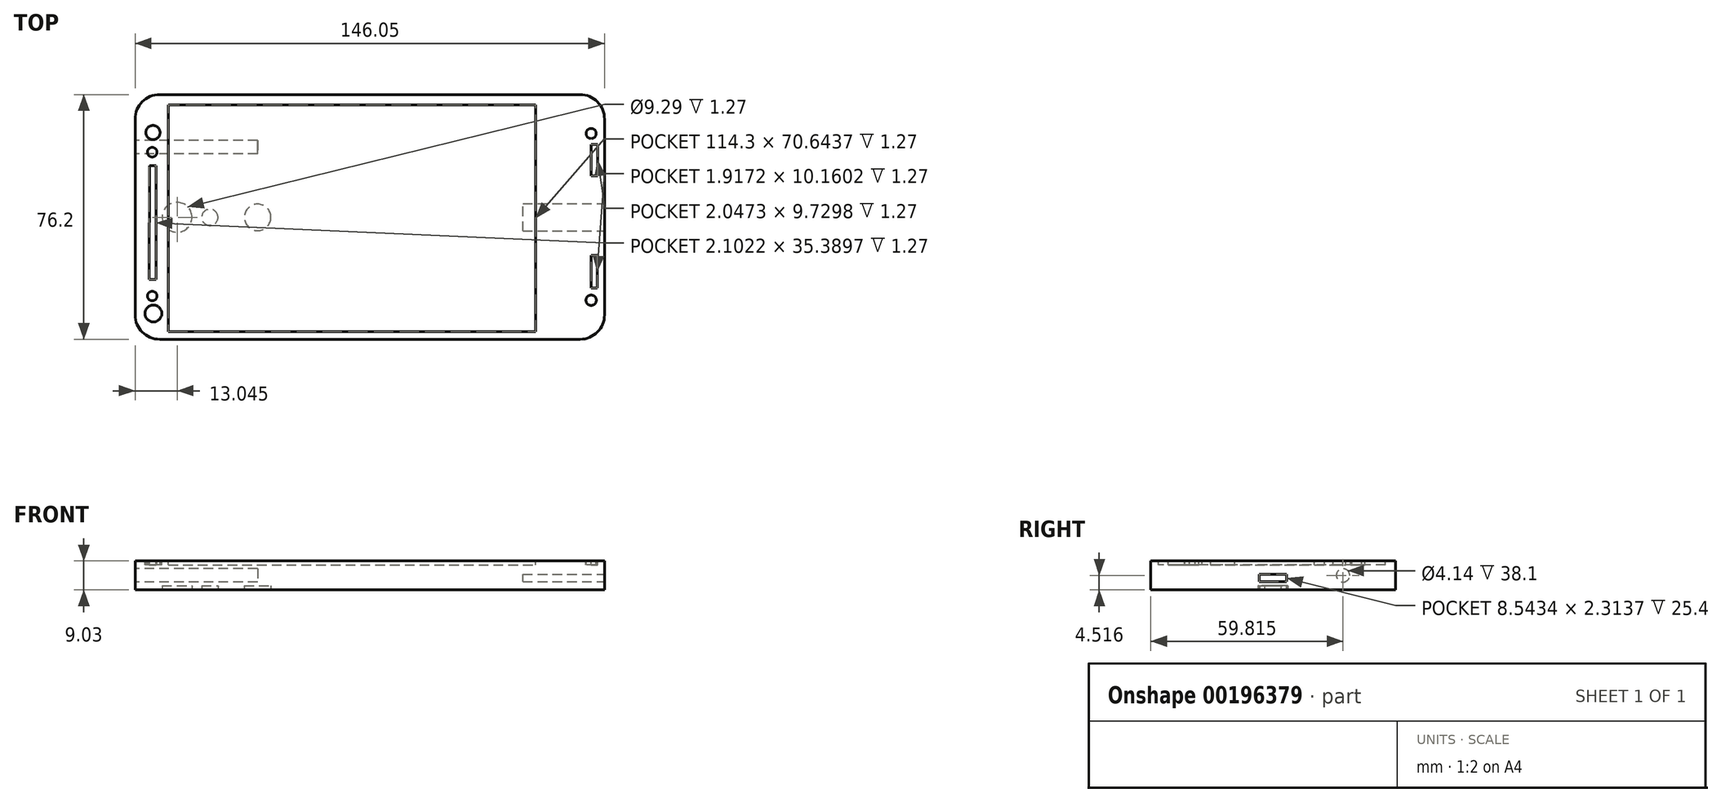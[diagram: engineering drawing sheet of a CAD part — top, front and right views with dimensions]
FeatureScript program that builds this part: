
annotation { "Feature Type Name" : "Feature", "Feature Type Description" : "" }
export const myFeature = defineFeature(function(context is Context, id is Id, definition is map)
    precondition{}
    {
        {
            var Q0;
            Q0=qCreatedBy(makeId("Top.planeOp"),FACE);
            var sketch = newSketch(context, id + "F0", { "sketchPlane" : qUnion([Q0])});
            skLineSegment(sketch, "E0.bottom", {"start": v(-70.09, 38.22) * mm, "end": v(75.96, 38.22) * mm});
            skLineSegment(sketch, "E0.top", {"start": v(-70.09, -37.98) * mm, "end": v(75.96, -37.98) * mm});
            skLineSegment(sketch, "E0.left", {"start": v(-70.09, 38.22) * mm, "end": v(-70.09, -37.98) * mm});
            skLineSegment(sketch, "E0.right", {"start": v(75.96, 38.22) * mm, "end": v(75.96, -37.98) * mm});
            skSolve(sketch);
        }
        {
            var Q0;
            Q0=qSketchRegion(id+"F0",true);
            extrude(context, id + "F1", {"entities" : qUnion([Q0]), "depth" : 9.03 * mm});
        }
        {
            var Q0;
            Q0=makeQuery(id+"F1.opExtrude","SWEPT_EDGE",EDGE,{"disambiguationData":[OSD([sQuery(id+"F0.wireOp",EDGE,"E0.top"),sQuery(id+"F0.wireOp",EDGE,"E0.right")])]});
            var Q1;
            Q1=makeQuery(id+"F1.opExtrude","SWEPT_EDGE",EDGE,{"disambiguationData":[OSD([sQuery(id+"F0.wireOp",EDGE,"E0.top"),sQuery(id+"F0.wireOp",EDGE,"E0.left")])]});
            var Q2;
            Q2=makeQuery(id+"F1.opExtrude","SWEPT_EDGE",EDGE,{"disambiguationData":[OSD([sQuery(id+"F0.wireOp",EDGE,"E0.bottom"),sQuery(id+"F0.wireOp",EDGE,"E0.left")])]});
            var Q3;
            Q3=makeQuery(id+"F1.opExtrude","SWEPT_EDGE",EDGE,{"disambiguationData":[OSD([sQuery(id+"F0.wireOp",EDGE,"E0.bottom"),sQuery(id+"F0.wireOp",EDGE,"E0.right")])]});
            fillet(context, id + "F2", {"entities" : qUnion([Q0, Q1, Q2, Q3]), "radius" : 7.62 * mm, "tangentPropagation" : true, "allowEdgeOverflow" : false});
        }
        {
            var Q0;
            Q0=makeQuery(id+"F1.opExtrude","SWEPT_FACE",FACE,{"disambiguationData":[OSD([sQuery(id+"F0.wireOp",EDGE,"E0.right")])]});
            var sketch = newSketch(context, id + "F3", { "sketchPlane" : qUnion([Q0])});
            skPoint(sketch, "E1.endSnap0", {"position": v(-30.36, 4.52) * mm});
            skLineSegment(sketch, "E2", {"start": v(-4.27, 2.5) * mm, "end": v(4.27, 2.5) * mm});
            skLineSegment(sketch, "E3", {"start": v(-4.27, 2.5) * mm, "end": v(-4.27, 4.81) * mm});
            skLineSegment(sketch, "E4", {"start": v(4.27, 2.5) * mm, "end": v(4.27, 4.81) * mm});
            skPoint(sketch, "E5.centerSnap0", {"position": v(0, 2.5) * mm});
            skLineSegment(sketch, "E6", {"start": v(-4.27, 4.81) * mm, "end": v(4.27, 4.81) * mm});
            skSolve(sketch);
        }
        {
            var Q0;
            Q0=qSketchRegion(id+"F3",true);
            extrude(context, id + "F4", {"entities" : qUnion([Q0]), "operationType" : NewBodyOperationType.REMOVE, "oppositeDirection" : true, "depth" : 25.4 * mm});
        }
        {
            var Q0;
            Q0=makeQuery(id+"F1.opExtrude","SWEPT_FACE",FACE,{"disambiguationData":[OSD([sQuery(id+"F0.wireOp",EDGE,"E0.left")])]});
            var sketch = newSketch(context, id + "F5", { "sketchPlane" : qUnion([Q0])});
            skCircle(sketch, "E7", {"center": v(-21.84, 4.52) * mm, "radius": 2.07 * mm});
            skPoint(sketch, "E7.centerSnap0", {"position": v(-30.6, 4.52) * mm});
            skSolve(sketch);
        }
        {
            var Q0;
            Q0=qSketchRegion(id+"F5",true);
            extrude(context, id + "F6", {"entities" : qUnion([Q0]), "operationType" : NewBodyOperationType.REMOVE, "oppositeDirection" : true, "depth" : 2.54 * mm});
        }
        {
            var Q0;
            Q0=qSketchRegion(id+"F5",true);
            extrude(context, id + "F7", {"entities" : qUnion([Q0]), "operationType" : NewBodyOperationType.REMOVE, "oppositeDirection" : true, "depth" : 38.1 * mm});
        }
        {
            var Q0;
            Q0=makeQuery(id+"F1.opExtrude","CAP_FACE",FACE,{"disambiguationData":[OSD([sQuery(id+"F0.wireOp",EDGE,"E0.bottom"),sQuery(id+"F0.wireOp",EDGE,"E0.top"),sQuery(id+"F0.wireOp",EDGE,"E0.left"),sQuery(id+"F0.wireOp",EDGE,"E0.right")])],"isStart":false});
            var sketch = newSketch(context, id + "F8", { "sketchPlane" : qUnion([Q0])});
            skLineSegment(sketch, "E8.bottom", {"start": v(-59.77, 35.04) * mm, "end": v(54.53, 35.04) * mm});
            skLineSegment(sketch, "E8.top", {"start": v(-59.77, -35.6) * mm, "end": v(54.53, -35.6) * mm});
            skLineSegment(sketch, "E8.left", {"start": v(-59.77, 35.04) * mm, "end": v(-59.77, -35.6) * mm});
            skLineSegment(sketch, "E8.right", {"start": v(54.53, 35.04) * mm, "end": v(54.53, -35.6) * mm});
            skSolve(sketch);
        }
        {
            var Q0;
            Q0=qSketchRegion(id+"F8",true);
            extrude(context, id + "F9", {"entities" : qUnion([Q0]), "operationType" : NewBodyOperationType.REMOVE, "oppositeDirection" : true, "depth" : 1.27 * mm});
        }
        {
            var Q0;
            Q0=makeQuery(id+"F1.opExtrude","CAP_FACE",FACE,{"disambiguationData":[OSD([sQuery(id+"F0.wireOp",EDGE,"E0.bottom"),sQuery(id+"F0.wireOp",EDGE,"E0.top"),sQuery(id+"F0.wireOp",EDGE,"E0.left"),sQuery(id+"F0.wireOp",EDGE,"E0.right")])],"isStart":false});
            var sketch = newSketch(context, id + "F10", { "sketchPlane" : qUnion([Q0])});
            skCircle(sketch, "E9", {"center": v(-64.55, 26.4) * mm, "radius": 2.21 * mm});
            skCircle(sketch, "E10", {"center": v(-64.78, 20.28) * mm, "radius": 1.5 * mm});
            skCircle(sketch, "E11", {"center": v(71.8, 26.1) * mm, "radius": 1.57 * mm});
            skCircle(sketch, "E12", {"center": v(71.8, -25.83) * mm, "radius": 1.61 * mm});
            skCircle(sketch, "E13", {"center": v(-64.42, -29.95) * mm, "radius": 2.61 * mm});
            skCircle(sketch, "E14", {"center": v(-64.78, -24.52) * mm, "radius": 1.48 * mm});
            skLineSegment(sketch, "E15", {"start": v(-65.67, 16.05) * mm, "end": v(-63.61, 16.05) * mm});
            skLineSegment(sketch, "E16", {"start": v(-63.61, 16.05) * mm, "end": v(-63.61, -19.34) * mm});
            skLineSegment(sketch, "E17", {"start": v(-63.61, -19.34) * mm, "end": v(-65.71, -19.34) * mm});
            skLineSegment(sketch, "E18", {"start": v(-65.71, -19.34) * mm, "end": v(-65.67, 16.05) * mm});
            skLineSegment(sketch, "E19", {"start": v(71.8, 22.68) * mm, "end": v(73.85, 22.68) * mm});
            skLineSegment(sketch, "E20", {"start": v(73.85, 22.68) * mm, "end": v(73.85, 12.95) * mm});
            skLineSegment(sketch, "E21", {"start": v(73.85, 12.95) * mm, "end": v(71.8, 12.95) * mm});
            skLineSegment(sketch, "E22", {"start": v(71.8, 12.95) * mm, "end": v(71.8, 22.68) * mm});
            skLineSegment(sketch, "E23", {"start": v(71.8, -22.01) * mm, "end": v(73.72, -22.01) * mm});
            skLineSegment(sketch, "E24", {"start": v(73.72, -22.01) * mm, "end": v(73.72, -11.85) * mm});
            skLineSegment(sketch, "E25", {"start": v(73.72, -11.85) * mm, "end": v(71.8, -11.85) * mm});
            skLineSegment(sketch, "E26", {"start": v(71.8, -11.85) * mm, "end": v(71.8, -22.01) * mm});
            skSolve(sketch);
        }
        {
            var Q0;
            Q0=qSketchRegion(id+"F10",true);
            extrude(context, id + "F11", {"entities" : qUnion([Q0]), "operationType" : NewBodyOperationType.REMOVE, "oppositeDirection" : true, "depth" : 1.27 * mm});
        }
        {
            var Q0;
            Q0=makeQuery(id+"F1.opExtrude","CAP_FACE",FACE,{"disambiguationData":[OSD([sQuery(id+"F0.wireOp",EDGE,"E0.bottom"),sQuery(id+"F0.wireOp",EDGE,"E0.top"),sQuery(id+"F0.wireOp",EDGE,"E0.left"),sQuery(id+"F0.wireOp",EDGE,"E0.right")])],"isStart":true});
            var sketch = newSketch(context, id + "F12", { "sketchPlane" : qUnion([Q0])});
            skCircle(sketch, "E27", {"center": v(-57.05, 0) * mm, "radius": 4.64 * mm});
            skCircle(sketch, "E28", {"center": v(-46.85, 0) * mm, "radius": 2.54 * mm});
            skCircle(sketch, "E29", {"center": v(-32, 0) * mm, "radius": 4.13 * mm});
            skSolve(sketch);
        }
        {
            var Q0;
            Q0=qSketchRegion(id+"F12",true);
            extrude(context, id + "F13", {"entities" : qUnion([Q0]), "operationType" : NewBodyOperationType.REMOVE, "oppositeDirection" : true, "depth" : 1.27 * mm});
        }
    });
